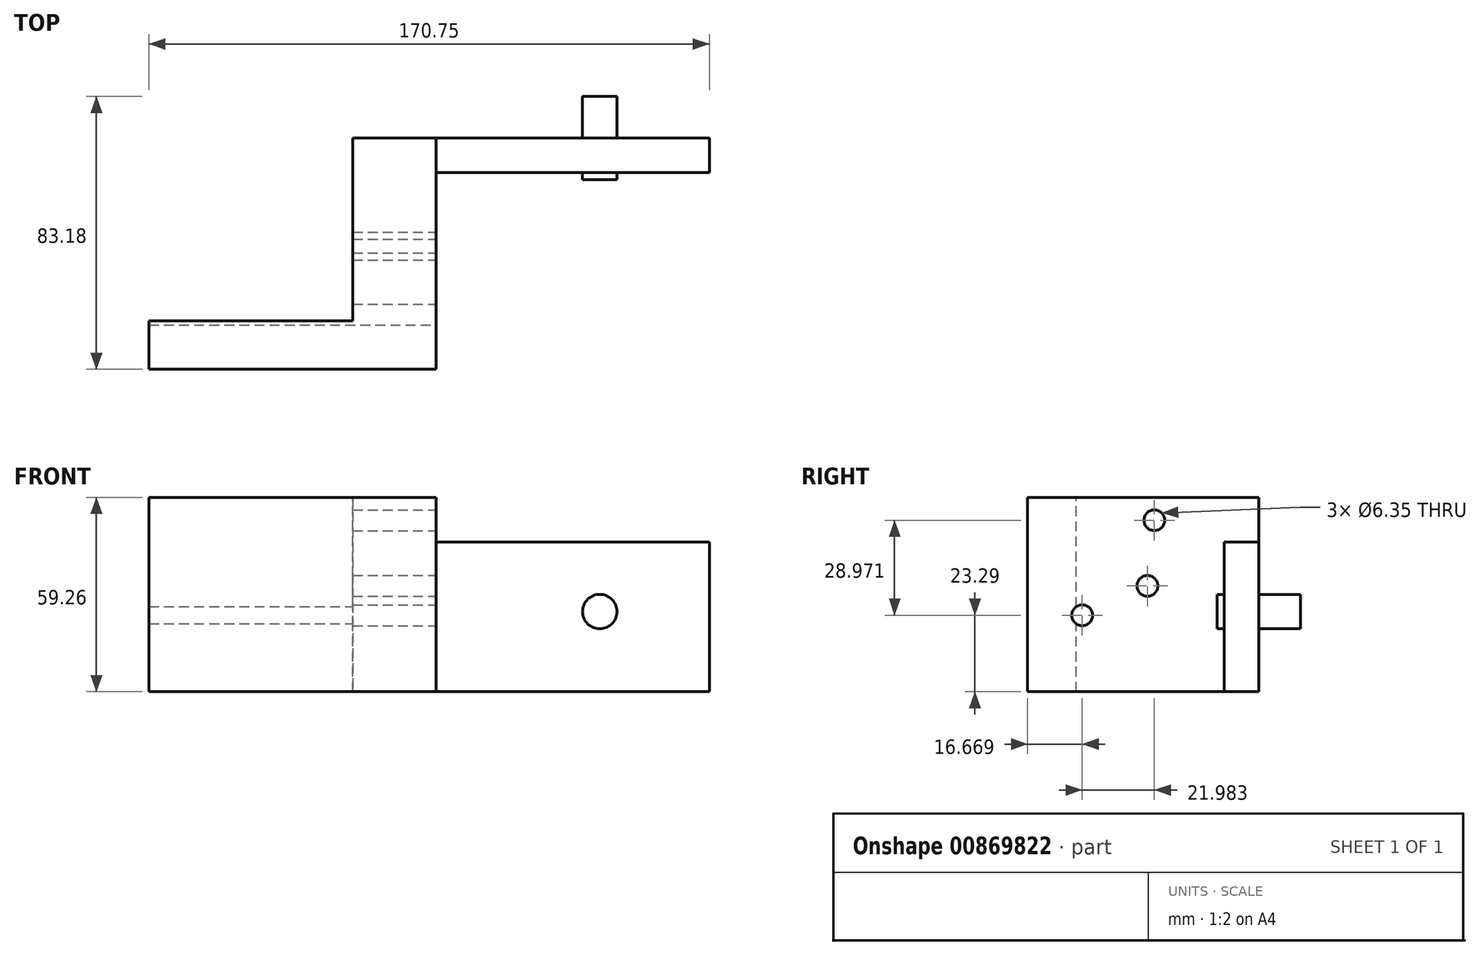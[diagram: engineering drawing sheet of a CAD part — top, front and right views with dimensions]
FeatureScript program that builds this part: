
annotation { "Feature Type Name" : "Feature", "Feature Type Description" : "" }
export const myFeature = defineFeature(function(context is Context, id is Id, definition is map)
    precondition{}
    {
        {
            var Q0;
            Q0=qCreatedBy(makeId("Front.planeOp"),FACE);
            var sketch = newSketch(context, id + "F0", { "sketchPlane" : qUnion([Q0])});
            skLineSegment(sketch, "E0.bottom", {"start": v(0, 0) * mm, "end": v(62.08, 0) * mm});
            skLineSegment(sketch, "E0.top", {"start": v(0, 59.26) * mm, "end": v(62.08, 59.26) * mm});
            skLineSegment(sketch, "E0.left", {"start": v(0, 0) * mm, "end": v(0, 59.26) * mm});
            skLineSegment(sketch, "E0.right", {"start": v(62.08, 0) * mm, "end": v(62.08, 59.26) * mm});
            skSolve(sketch);
        }
        {
            var Q0;
            Q0=makeQuery(id+"F0.imprint","IMPRINT",FACE,{"disambiguationData":[TD([[makeQuery(id+"F0.imprint","IMPRINT",EDGE,{"derivedFrom":sQuery(id+"F0.wireOp",EDGE,"E0.bottom")}),1.0]])]});
            extrude(context, id + "F1", {"entities" : qUnion([Q0]), "oppositeDirection" : true, "depth" : 14.82 * mm, "offsetDistance" : 25.4 * mm});
        }
        {
            var Q0;
            Q0=makeQuery(id+"F1.opExtrude","SWEPT_FACE",FACE,{"disambiguationData":[OSD([sQuery(id+"F0.wireOp",EDGE,"E0.right")])]});
            var sketch = newSketch(context, id + "F2", { "sketchPlane" : qUnion([Q0])});
            skLineSegment(sketch, "E1.bottom", {"start": v(0, 59.26) * mm, "end": v(70.48, 59.26) * mm});
            skLineSegment(sketch, "E1.top", {"start": v(0, 0) * mm, "end": v(70.48, 0) * mm});
            skLineSegment(sketch, "E1.left", {"start": v(0, 59.26) * mm, "end": v(0, 0) * mm});
            skLineSegment(sketch, "E1.right", {"start": v(70.48, 59.26) * mm, "end": v(70.48, 0) * mm});
            skSolve(sketch);
        }
        {
            var Q0;
            Q0 = qSketchRegion(id + "F2", true);
            extrude(context, id + "F3", {"entities" : qUnion([Q0]), "operationType" : NewBodyOperationType.ADD, "depth" : 25.4 * mm, "offsetDistance" : 25.4 * mm});
        }
        {
            var Q0;
            Q0=makeQuery(id+"F3.opExtrude","CAP_FACE",FACE,{"disambiguationData":[OSD([sQuery(id+"F2.wireOp",EDGE,"E1.bottom"),sQuery(id+"F2.wireOp",EDGE,"E1.top"),sQuery(id+"F2.wireOp",EDGE,"E1.left"),sQuery(id+"F2.wireOp",EDGE,"E1.right")])],"isStart":false});
            var sketch = newSketch(context, id + "F4", { "sketchPlane" : qUnion([Q0])});
            skLineSegment(sketch, "E2.bottom", {"start": v(59.98, 45.62) * mm, "end": v(70.48, 45.62) * mm});
            skLineSegment(sketch, "E2.top", {"start": v(59.98, 0) * mm, "end": v(70.48, 0) * mm});
            skLineSegment(sketch, "E2.left", {"start": v(59.98, 45.62) * mm, "end": v(59.98, 0) * mm});
            skLineSegment(sketch, "E2.right", {"start": v(70.48, 45.62) * mm, "end": v(70.48, 0) * mm});
            skSolve(sketch);
        }
        {
            var Q0;
            Q0 = qSketchRegion(id + "F4", true);
            extrude(context, id + "F5", {"entities" : qUnion([Q0]), "operationType" : NewBodyOperationType.ADD, "depth" : 83.28 * mm, "offsetDistance" : 25.4 * mm});
        }
        {
            var Q0;
            Q0=makeQuery(id+"F5.boolean.opBoolean","MERGE",FACE,{"derivedFrom":[makeQuery(id+"F3.opExtrude","SWEPT_FACE",FACE,{"disambiguationData":[OSD([sQuery(id+"F2.wireOp",EDGE,"E1.right")])]}),makeQuery(id+"F5.opExtrude","SWEPT_FACE",FACE,{"disambiguationData":[OSD([sQuery(id+"F4.wireOp",EDGE,"E2.right")])]})]});
            var sketch = newSketch(context, id + "F6", { "sketchPlane" : qUnion([Q0])});
            skCircle(sketch, "E3", {"center": v(-137.37, 24.4) * mm, "radius": 5.26 * mm});
            skSolve(sketch);
        }
        {
            var Q0;
            Q0 = qSketchRegion(id + "F6", true);
            extrude(context, id + "F7", {"entities" : qUnion([Q0]), "operationType" : NewBodyOperationType.ADD, "endBound" : BoundingType.SYMMETRIC, "depth" : 25.4 * mm, "offsetDistance" : 25.4 * mm});
        }
        {
            var Q0;
            Q0=makeQuery(id+"F3.opExtrude","CAP_FACE",FACE,{"disambiguationData":[OSD([sQuery(id+"F2.wireOp",EDGE,"E1.bottom"),sQuery(id+"F2.wireOp",EDGE,"E1.top"),sQuery(id+"F2.wireOp",EDGE,"E1.left"),sQuery(id+"F2.wireOp",EDGE,"E1.right")])],"isStart":false});
            var sketch = newSketch(context, id + "F8", { "sketchPlane" : qUnion([Q0])});
            skPoint(sketch, "E4", {"position": v(36.53, 32.23) * mm});
            skPoint(sketch, "E5", {"position": v(38.65, 52.26) * mm});
            skPoint(sketch, "E6", {"position": v(16.67, 23.3) * mm});
            skSolve(sketch);
        }
        {
            var Q0;
            Q0=sQuery(id+"F8.wireOp",VERTEX,"E6");
            var Q1;
            Q1=sQuery(id+"F8.wireOp",VERTEX,"E4");
            var Q2;
            Q2=sQuery(id+"F8.wireOp",VERTEX,"E5");
            var Q3;
            Q3=makeQuery(id+"F1.opExtrude","SWEPT_BODY",BODY,{"disambiguationData":[OSD([sQuery(id+"F0.wireOp",EDGE,"E0.bottom"),sQuery(id+"F0.wireOp",EDGE,"E0.top"),sQuery(id+"F0.wireOp",EDGE,"E0.left"),sQuery(id+"F0.wireOp",EDGE,"E0.right")])]});
            hole(context, id + "F9", {"style" : HoleStyle.SIMPLE, "endStyle" : HoleEndStyle.THROUGH, "holeDiameter" : 6.35 * mm, "majorDiameter" : 6.35 * mm, "isTappedThrough" : true, "tappedDepth" : 12.7 * mm, "tapClearance" : 3, "locations" : qUnion([Q0, Q1, Q2]), "scope" : qUnion([Q3])});
        }
    });
